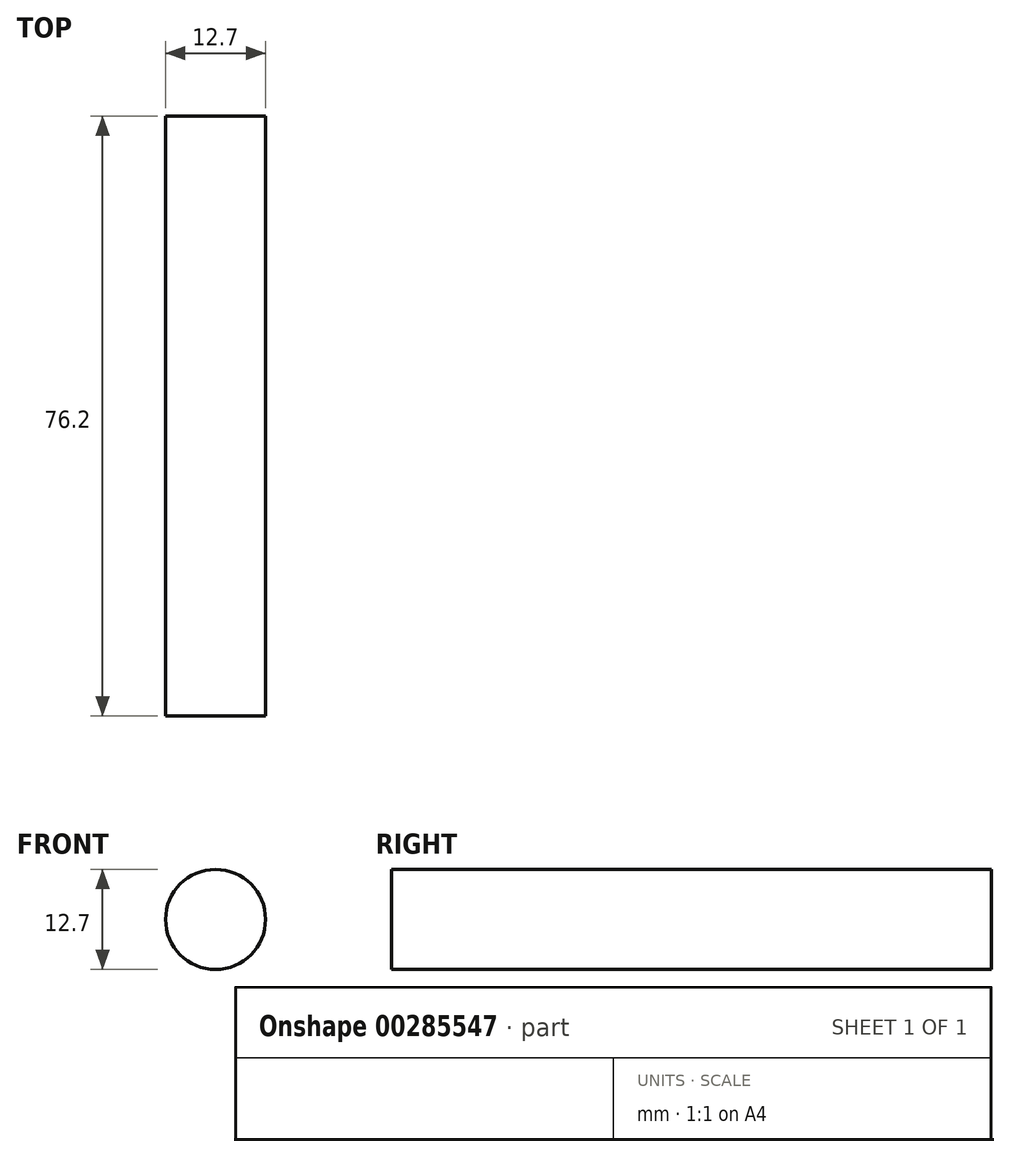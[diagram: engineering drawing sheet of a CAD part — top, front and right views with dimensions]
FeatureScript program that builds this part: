
annotation { "Feature Type Name" : "Feature", "Feature Type Description" : "" }
export const myFeature = defineFeature(function(context is Context, id is Id, definition is map)
    precondition{}
    {
        {
            var Q0;
            Q0=qCreatedBy(makeId("Front.planeOp"),FACE);
            var sketch = newSketch(context, id + "F0", { "sketchPlane" : qUnion([Q0])});
            skCircle(sketch, "E0", {"center": v(0, 0) * mm, "radius": 6.35 * mm});
            skSolve(sketch);
        }
        {
            var Q0;
            Q0=makeQuery(id+"F0.imprint","IMPRINT",FACE,{"disambiguationData":[TD([[makeQuery(id+"F0.imprint","IMPRINT",EDGE,{"derivedFrom":sQuery(id+"F0.wireOp",EDGE,"E0")}),1.0]])]});
            extrude(context, id + "F1", {"entities" : qUnion([Q0]), "depth" : 76.2 * mm});
        }
    });
